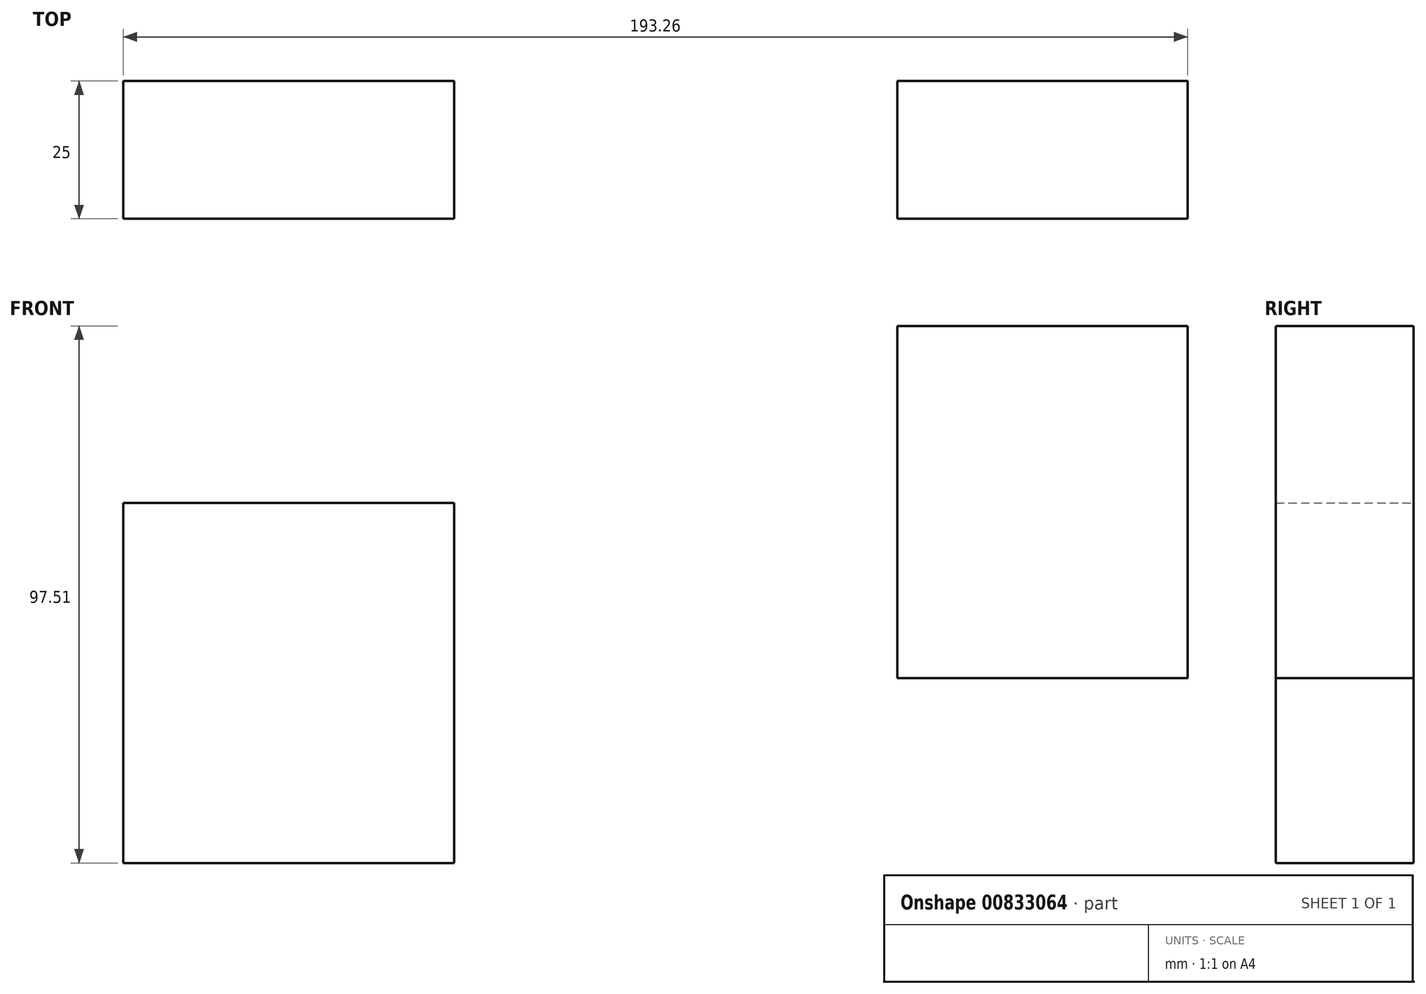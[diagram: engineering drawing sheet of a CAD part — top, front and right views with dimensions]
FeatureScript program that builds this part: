
annotation { "Feature Type Name" : "Feature", "Feature Type Description" : "" }
export const myFeature = defineFeature(function(context is Context, id is Id, definition is map)
    precondition{}
    {
        {
            var Q0;
            Q0=qCreatedBy(makeId("Front.planeOp"),FACE);
            var sketch = newSketch(context, id + "F0", { "sketchPlane" : qUnion([Q0])});
            skLineSegment(sketch, "E0.bottom", {"start": v(-143.36, 3.18) * mm, "end": v(-83.28, 3.18) * mm});
            skLineSegment(sketch, "E0.top", {"start": v(-143.36, 68.59) * mm, "end": v(-83.28, 68.59) * mm});
            skLineSegment(sketch, "E0.left", {"start": v(-143.36, 3.18) * mm, "end": v(-143.36, 68.59) * mm});
            skLineSegment(sketch, "E0.right", {"start": v(-83.28, 3.18) * mm, "end": v(-83.28, 68.59) * mm});
            skPoint(sketch, "E0.middle", {"position": v(-113.32, 35.88) * mm});
            skLineSegment(sketch, "E1.bottom", {"start": v(-2.84, 36.73) * mm, "end": v(49.9, 36.73) * mm});
            skLineSegment(sketch, "E1.top", {"start": v(-2.84, 100.69) * mm, "end": v(49.9, 100.69) * mm});
            skLineSegment(sketch, "E1.left", {"start": v(-2.84, 36.73) * mm, "end": v(-2.84, 100.69) * mm});
            skLineSegment(sketch, "E1.right", {"start": v(49.9, 36.73) * mm, "end": v(49.9, 100.69) * mm});
            skPoint(sketch, "E1.middle", {"position": v(23.53, 68.71) * mm});
            skSolve(sketch);
        }
        {
            var Q0;
            Q0=makeQuery(id+"F0.imprint","IMPRINT",FACE,{"disambiguationData":[TD([[makeQuery(id+"F0.imprint","IMPRINT",EDGE,{"derivedFrom":sQuery(id+"F0.wireOp",EDGE,"E0.bottom")}),1.0]])]});
            var Q1;
            Q1=makeQuery(id+"F0.imprint","IMPRINT",FACE,{"disambiguationData":[TD([[makeQuery(id+"F0.imprint","IMPRINT",EDGE,{"derivedFrom":sQuery(id+"F0.wireOp",EDGE,"E1.bottom")}),1.0]])]});
            extrude(context, id + "F1", {"entities" : qUnion([Q0, Q1]), "depth" : 25 * mm, "offsetDistance" : 25 * mm});
        }
    });
